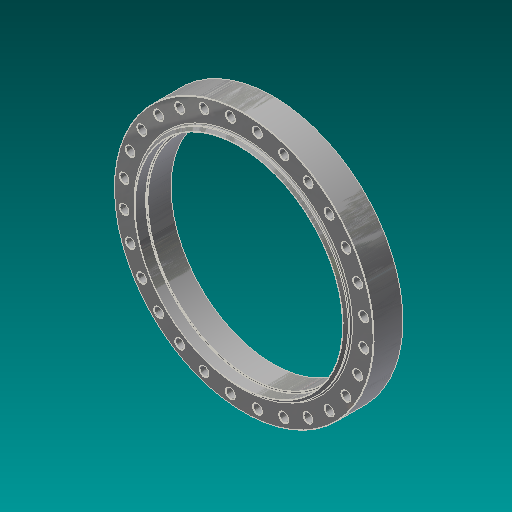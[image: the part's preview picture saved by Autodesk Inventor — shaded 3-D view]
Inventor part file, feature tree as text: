
AUTODESK INVENTOR PART (.ipt)
format: ipt  version: 2017.3 (Build 213257000, 257)  size: 331,264 bytes
history: native  units: in
note: dims shown in document units (in); Inventor stores cm internally (conversion verified against a paired STEP export)
features: chamfer x3, sketch x3, revolve x1, hole x1, pattern_circular x1, extrude x1, fillet x1
ambient origin geometry x8: Origin, YZ Plane, XZ Plane, XY Plane, X Axis, Y Axis, Z Axis, Center Point
bodies: Solid1 (feature_tree)
feature tree (11):
  revolve  "Revolution1"  [1 undecoded]
  hole  "Hole1"  [1 undecoded]
  chamfer  "Chamfer1"  Distance=32.0in
  pattern_circular  "Circular Pattern1"  [2 undecoded]
  chamfer  "Chamfer2"  Distance=32.0in
  extrude  "Extrusion1"  Depth=0.0312in
  fillet  "Fillet1"  Radius=0.4375in
  chamfer  "Chamfer3"  Distance=0.2in
  sketch  "Sketch1"  dims[d0=5.125in d1=38.75in]
  sketch  "Sketch2"  dims[d2=4.375in d3=33.75in]
  sketch  "Sketch3"  dims[d4=0.0625in d5=32.0in d6=31.0in d7=32.0in d8=0.2577in d9=0.4375in d10=0.2in d11=90.0deg d12=36.0in d13=0.0442in d14=1.375in d15=0.75in d16=0.375in d17=0.25in d18=0.5635in d19=1.0in d20=0.8108in d21=0.0625in d22=0.125in d23=45.0deg d24=11.0236in d25=360.0deg d27=0.0625in d28=0.125in d29=45.0deg d30=30.5in d31=3.5in d32=0.0in d33=0.0312in d34=0.0312in d35=0.125in d36=45.0deg]
note: 4 required parameter values undecoded (feature->parameter linkage not recoverable at this tier; creation-order binding heuristic only, values carry confidence <= 0.55)